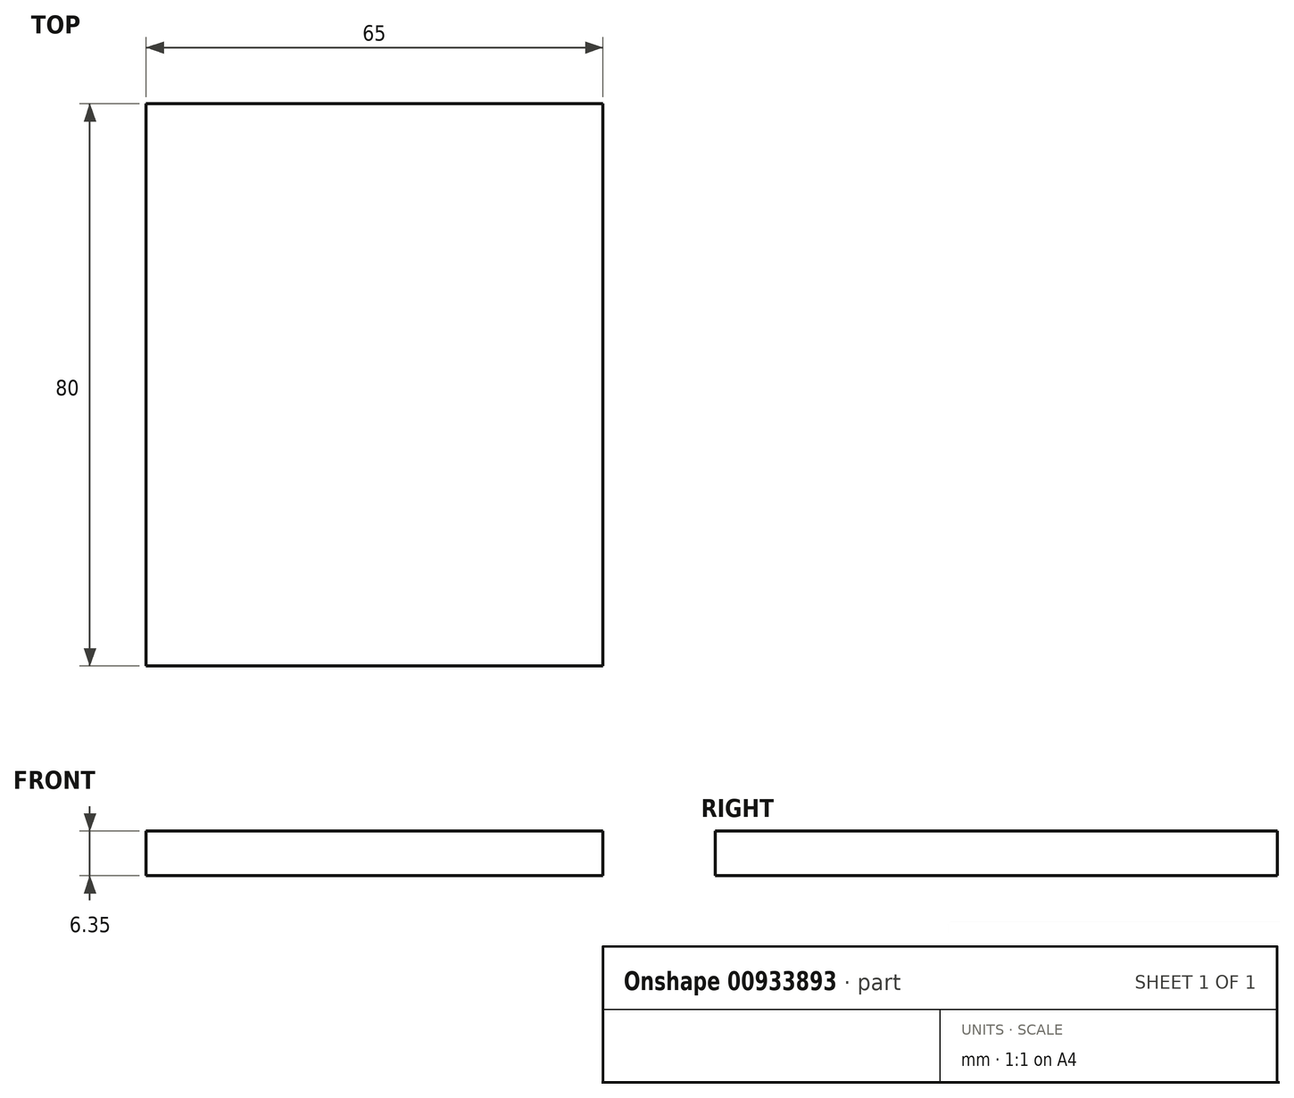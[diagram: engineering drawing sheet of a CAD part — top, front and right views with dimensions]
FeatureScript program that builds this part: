
annotation { "Feature Type Name" : "Feature", "Feature Type Description" : "" }
export const myFeature = defineFeature(function(context is Context, id is Id, definition is map)
    precondition{}
    {
        {
            var Q0;
            Q0=qCreatedBy(makeId("Top.planeOp"),FACE);
            var sketch = newSketch(context, id + "F0", { "sketchPlane" : qUnion([Q0])});
            skLineSegment(sketch, "E0.bottom", {"start": v(0, 0) * mm, "end": v(65, 0) * mm});
            skLineSegment(sketch, "E0.top", {"start": v(0, 80) * mm, "end": v(65, 80) * mm});
            skLineSegment(sketch, "E0.left", {"start": v(0, 0) * mm, "end": v(0, 80) * mm});
            skLineSegment(sketch, "E0.right", {"start": v(65, 0) * mm, "end": v(65, 80) * mm});
            skSolve(sketch);
        }
        {
            var Q0;
            Q0 = qSketchRegion(id + "F0", true);
            extrude(context, id + "F1", {"entities" : qUnion([Q0]), "depth" : 6.35 * mm, "offsetDistance" : 25.4 * mm});
        }
    });
